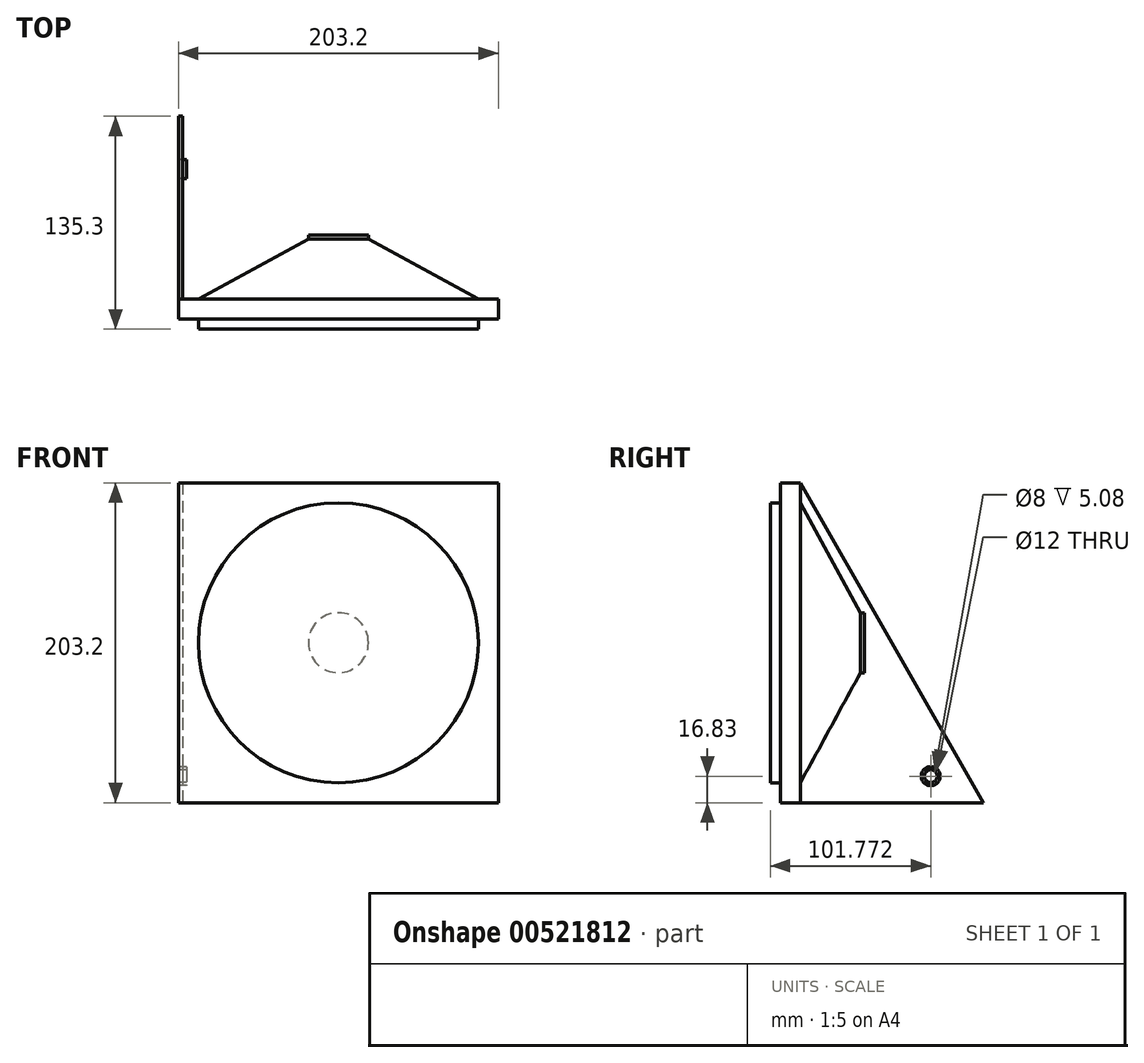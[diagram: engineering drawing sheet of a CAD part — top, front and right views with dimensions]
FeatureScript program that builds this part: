
annotation { "Feature Type Name" : "Feature", "Feature Type Description" : "" }
export const myFeature = defineFeature(function(context is Context, id is Id, definition is map)
    precondition{}
    {
        {
            var Q0;
            Q0=qCreatedBy(makeId("Front.planeOp"),FACE);
            var sketch = newSketch(context, id + "F0", { "sketchPlane" : qUnion([Q0])});
            skLineSegment(sketch, "E0.bottom", {"start": v(101.6, 101.6) * mm, "end": v(-101.6, 101.6) * mm});
            skLineSegment(sketch, "E0.top", {"start": v(101.6, -101.6) * mm, "end": v(-101.6, -101.6) * mm});
            skLineSegment(sketch, "E0.left", {"start": v(101.6, 101.6) * mm, "end": v(101.6, -101.6) * mm});
            skLineSegment(sketch, "E0.right", {"start": v(-101.6, 101.6) * mm, "end": v(-101.6, -101.6) * mm});
            skPoint(sketch, "E0.middle", {"position": v(0, 0) * mm});
            skCircle(sketch, "E1", {"center": v(0, 0) * mm, "radius": 88.9 * mm});
            skLineSegment(sketch, "E2", {"start": v(0, 101.6) * mm, "end": v(0, -101.6) * mm, "construction": true});
            skSolve(sketch);
        }
        {
            var Q0;
            Q0=makeQuery(id+"F0.imprint","IMPRINT",FACE,{"disambiguationData":[TD([[makeQuery(id+"F0.imprint","IMPRINT",EDGE,{"derivedFrom":sQuery(id+"F0.wireOp",EDGE,"E0.bottom")}),1.0]])]});
            var Q1;
            Q1=makeQuery(id+"F0.imprint","IMPRINT",FACE,{"disambiguationData":[TD([[makeQuery(id+"F0.imprint","IMPRINT",EDGE,{"derivedFrom":sQuery(id+"F0.wireOp",EDGE,"E1")}),1.0]])]});
            extrude(context, id + "F1", {"entities" : qUnion([Q0, Q1]), "depth" : 12.7 * mm, "offsetDistance" : 25.4 * mm});
        }
        {
            var Q0;
            Q0=makeQuery(id+"F0.imprint","IMPRINT",FACE,{"disambiguationData":[TD([[makeQuery(id+"F0.imprint","IMPRINT",EDGE,{"derivedFrom":sQuery(id+"F0.wireOp",EDGE,"E1")}),1.0]])]});
            extrude(context, id + "F2", {"entities" : qUnion([Q0]), "operationType" : NewBodyOperationType.ADD, "depth" : 19.05 * mm, "offsetDistance" : 25.4 * mm});
        }
        {
            var Q0;
            Q0=makeQuery(id+"F1.opExtrude","SWEPT_FACE",FACE,{"disambiguationData":[OSD([sQuery(id+"F0.wireOp",EDGE,"E0.right")])]});
            var sketch = newSketch(context, id + "F3", { "sketchPlane" : qUnion([Q0])});
            skLineSegment(sketch, "E3", {"start": v(0, -101.6) * mm, "end": v(-116.25, -101.6) * mm});
            skLineSegment(sketch, "E4", {"start": v(-116.25, -101.6) * mm, "end": v(0, 101.6) * mm});
            skCircle(sketch, "E5", {"center": v(-82.72, -84.77) * mm, "radius": 6 * mm});
            skCircle(sketch, "E6", {"center": v(-82.72, -84.77) * mm, "radius": 4 * mm});
            skSolve(sketch);
        }
        {
            var Q0;
            Q0=makeQuery(id+"F3.imprint","IMPRINT",FACE,{"disambiguationData":[TD([[makeQuery(id+"F3.imprint","IMPRINT",EDGE,{"derivedFrom":sQuery(id+"F3.wireOp",EDGE,"E3")}),-1.0]])]});
            extrude(context, id + "F4", {"entities" : qUnion([Q0]), "operationType" : NewBodyOperationType.ADD, "oppositeDirection" : true, "depth" : 2.54 * mm, "offsetDistance" : 25.4 * mm});
        }
        {
            var Q0;
            Q0=makeQuery(id+"F3.imprint","IMPRINT",FACE,{"disambiguationData":[TD([[makeQuery(id+"F3.imprint","IMPRINT",EDGE,{"derivedFrom":sQuery(id+"F3.wireOp",EDGE,"E5")}),1.0]])]});
            extrude(context, id + "F5", {"entities" : qUnion([Q0]), "oppositeDirection" : true, "depth" : 5.08 * mm, "offsetDistance" : 25.4 * mm});
        }
        {
            var Q0;
            Q0=makeQuery(id+"F0.imprint","IMPRINT",FACE,{"disambiguationData":[TD([[makeQuery(id+"F0.imprint","IMPRINT",EDGE,{"derivedFrom":sQuery(id+"F0.wireOp",EDGE,"E0.bottom")}),1.0]])]});
            cPlane(context, id + "F6", {"entities" : qUnion([Q0]), "cplaneType" : CPlaneType.OFFSET, "offset" : 38.1 * mm, "oppositeDirection" : true, "width" : 152.4 * mm, "height" : 152.4 * mm});
        }
        {
            var Q0;
            Q0=qCreatedBy(id+"F6.planeOp",FACE);
            var sketch = newSketch(context, id + "F7", { "sketchPlane" : qUnion([Q0])});
            skCircle(sketch, "E7", {"center": v(0, 0) * mm, "radius": 19.05 * mm});
            skSolve(sketch);
        }
        {
            var Q1;
            Q1=makeQuery(id+"F0.imprint","IMPRINT",FACE,{"disambiguationData":[TD([[makeQuery(id+"F0.imprint","IMPRINT",EDGE,{"derivedFrom":sQuery(id+"F0.wireOp",EDGE,"E1")}),1.0]])]});
            var Q2;
            Q2=makeQuery(id+"F7.imprint","IMPRINT",FACE,{"disambiguationData":[TD([[makeQuery(id+"F7.imprint","IMPRINT",EDGE,{"derivedFrom":sQuery(id+"F7.wireOp",EDGE,"E7")}),1.0]])]});
            loft(context, id + "F8", {"operationType" : NewBodyOperationType.ADD, "sheetProfilesArray" : [{ "sheetProfileEntities" : qUnion([Q1]) }, { "sheetProfileEntities" : qUnion([Q2]) }]});
        }
        {
            var Q0;
            Q0=makeQuery(id+"F8.opLoft","CAP_FACE",FACE,{"disambiguationData":[OSD([makeQuery(id+"F7.imprint","IMPRINT",FACE,{"disambiguationData":[TD([[makeQuery(id+"F7.imprint","IMPRINT",EDGE,{"derivedFrom":sQuery(id+"F7.wireOp",EDGE,"E7")}),1.0]])]})])],"isStart":true});
            extrude(context, id + "F9", {"entities" : qUnion([Q0]), "operationType" : NewBodyOperationType.ADD, "depth" : 2.54 * mm, "offsetDistance" : 25.4 * mm});
        }
    });
